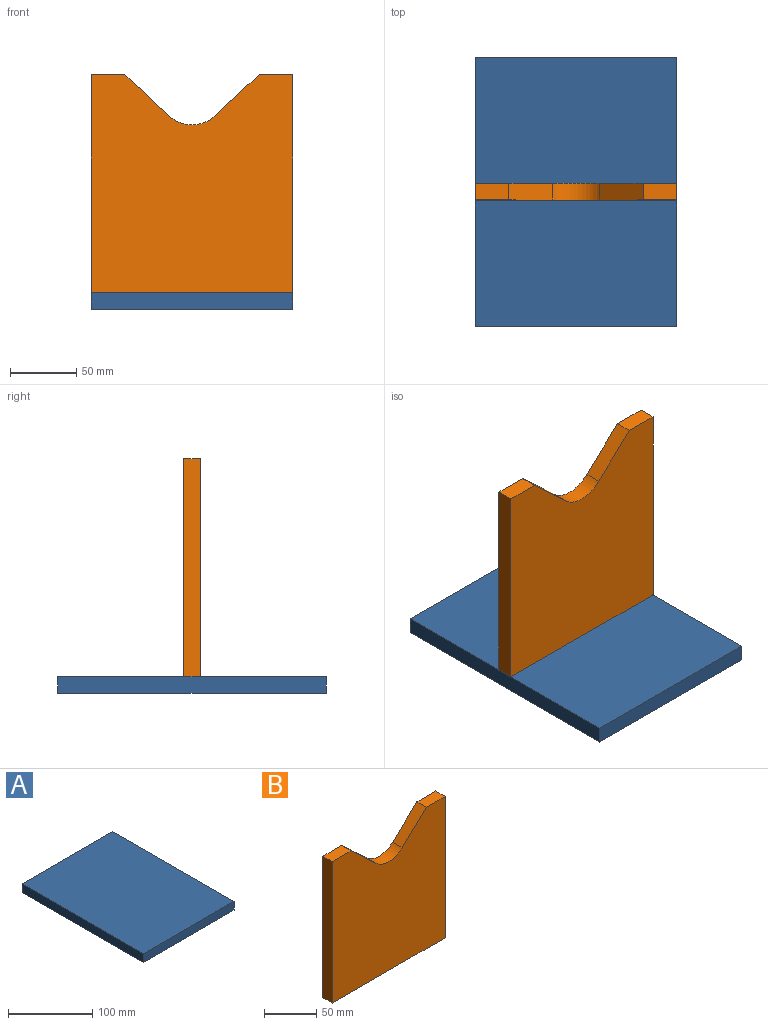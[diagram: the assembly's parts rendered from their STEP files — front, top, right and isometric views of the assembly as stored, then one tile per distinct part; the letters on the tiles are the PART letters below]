
ASSEMBLY  parts=2 mates=1
PART A: 6 faces, bbox 152.4x203.2x12.7 mm
  f0: plane 152.4x12.7mm, normal (0,1,0), area 1935.5mm2, adj f1,f3,f4,f5
  f1: plane 203.2x12.7mm, normal (-1,0,0), area 2580.6mm2, adj f0,f2,f4,f5
  f2: plane 152.4x12.7mm, normal (0,-1,0), area 1935.5mm2, adj f1,f3,f4,f5
  f3: plane 203.2x12.7mm, normal (1,0,0), area 2580.6mm2, adj f0,f2,f4,f5
  f4: plane 203.2x152.4mm, normal (0,0,1), area 30967.7mm2, adj f0,f1,f2,f3
  f5: plane 203.2x152.4mm, normal (0,0,-1), area 30967.7mm2, adj f0,f1,f2,f3
PART B: 10 faces, bbox 152.4x12.7x165.1 mm
  f0: plane 25.4x12.7mm, normal (0,0,1), area 322.6mm2, adj f1,f7,f8,f9
  f1: plane 165.1x12.7mm, normal (-1,0,0), area 2096.8mm2, adj f0,f2,f8,f9
  f2: plane 152.4x12.7mm, normal (0,0,-1), area 1935.5mm2, adj f1,f3,f8,f9
  f3: plane 165.1x12.7mm, normal (1,0,0), area 2096.8mm2, adj f2,f4,f8,f9
  f4: plane 25.4x12.7mm, normal (0,0,1), area 322.6mm2, adj f3,f5,f8,f9
  f5: plane 32.83x30.65mm, normal (-0.68,0,0.73), area 570.5mm2, adj f4,f6,f8,f9
  f6: cylinder r=25.4mm len=35.51mm, axis (0,1,0), area 499.4mm2, adj f5,f7,f8,f9
  f7: plane 33.26x31.07mm, normal (0.68,0,0.73), area 578mm2, adj f0,f6,f8,f9
  f8: plane 165.1x152.4mm, normal (0,-1,0), area 22868.6mm2, adj f0,f1,f2,f3,f4,f5,f6,f7
  f9: plane 165.1x152.4mm, normal (0,1,0), area 22868.6mm2, adj f0,f1,f2,f3,f4,f5,f6,f7
PLACE A t=(4.91,5.65,-6.44)mm
PLACE B t=(4.79,7.33,-46.26)mm
MATE fastened B.f3 <-> A.f3  axis (1,0,0) through (78,0.98,6.26)mm
